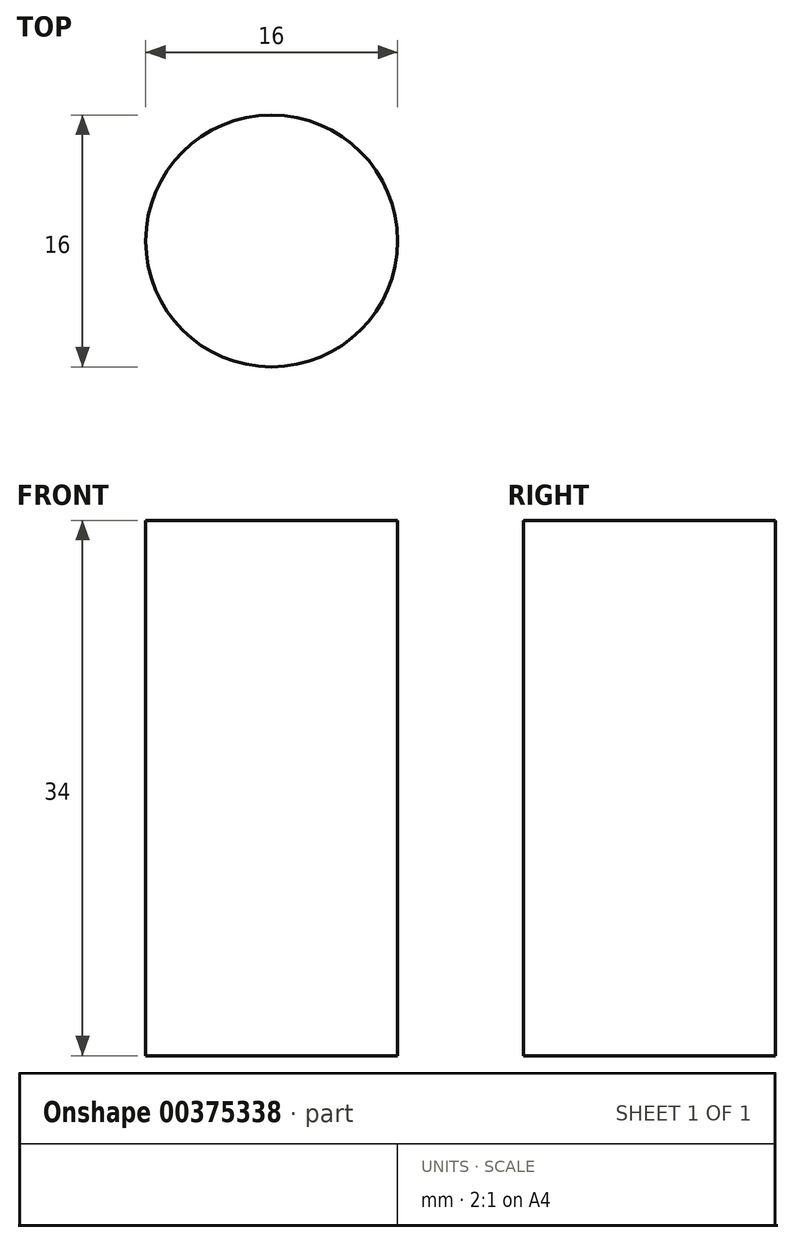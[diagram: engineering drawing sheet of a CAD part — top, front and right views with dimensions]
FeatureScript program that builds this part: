
annotation { "Feature Type Name" : "Feature", "Feature Type Description" : "" }
export const myFeature = defineFeature(function(context is Context, id is Id, definition is map)
    precondition{}
    {
        {
            var Q0;
            Q0=qCreatedBy(makeId("Top.planeOp"),FACE);
            var sketch = newSketch(context, id + "F0", { "sketchPlane" : qUnion([Q0])});
            skCircle(sketch, "E0", {"center": v(0, 0) * mm, "radius": 8 * mm});
            skSolve(sketch);
        }
        {
            var Q0;
            Q0=makeQuery(id+"F0.imprint","IMPRINT",FACE,{"disambiguationData":[TD([[makeQuery(id+"F0.imprint","IMPRINT",EDGE,{"derivedFrom":sQuery(id+"F0.wireOp",EDGE,"E0")}),1.0]])]});
            extrude(context, id + "F1", {"entities" : qUnion([Q0]), "depth" : 34 * mm});
        }
    });
